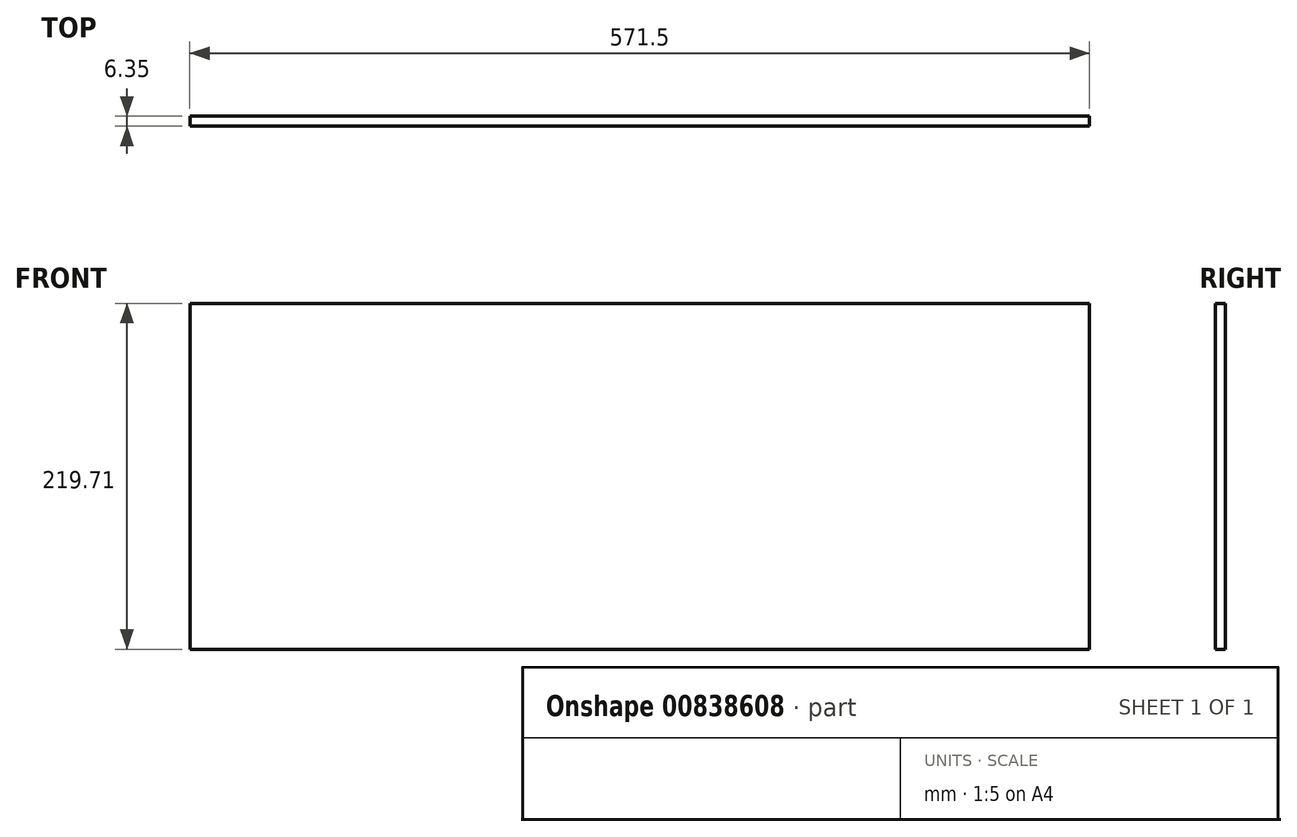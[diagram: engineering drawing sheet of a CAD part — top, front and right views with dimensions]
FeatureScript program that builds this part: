
annotation { "Feature Type Name" : "Feature", "Feature Type Description" : "" }
export const myFeature = defineFeature(function(context is Context, id is Id, definition is map)
    precondition{}
    {
        {
            var Q0;
            Q0=qCreatedBy(makeId("Front.planeOp"),FACE);
            var sketch = newSketch(context, id + "F0", { "sketchPlane" : qUnion([Q0])});
            skLineSegment(sketch, "E0.bottom", {"start": v(-290.57, 105.94) * mm, "end": v(280.93, 105.94) * mm});
            skLineSegment(sketch, "E0.top", {"start": v(-290.57, -113.77) * mm, "end": v(280.93, -113.77) * mm});
            skLineSegment(sketch, "E0.left", {"start": v(-290.57, 105.94) * mm, "end": v(-290.57, -113.77) * mm});
            skLineSegment(sketch, "E0.right", {"start": v(280.93, 105.94) * mm, "end": v(280.93, -113.77) * mm});
            skSolve(sketch);
        }
        {
            var Q0;
            Q0=makeQuery(id+"F0.imprint","IMPRINT",FACE,{"disambiguationData":[TD([[makeQuery(id+"F0.imprint","IMPRINT",EDGE,{"derivedFrom":sQuery(id+"F0.wireOp",EDGE,"E0.bottom")}),-1.0]])]});
            extrude(context, id + "F1", {"entities" : qUnion([Q0]), "depth" : 6.35 * mm, "offsetDistance" : 25.4 * mm});
        }
    });
